# Revit family: Drapery_Track-Lutron-Curved-Ceiling_Recessed_Mount new
name_source: partatom
category: Specialty Equipment
revit_build: Autodesk Revit 2017 (Build: 20160225_1515(x64)
units: mm (PartAtom-declared; Revit-internal decimal feet)

## family parameters
Cut with Voids When Loaded = Yes
Host = Face
OmniClass Number = 23.30.60.14.21
OmniClass Title = Shades
Part Type = Normal
Room Calculation Point = No
Round Connector Dimension = Use Diameter
Shared = No

## types (6) — shared parameters
Apparent Load = 0 VA
Assembly Code = E2010320
C Recessed Ends = 0' - 0 39/64"
Default Elevation = 0' - 0"
Electronic Drive Unit D105 = Yes
Electronic Drive Unit D145 = No
Electronic Drive Unit D175 = No
Electronic Drive Unit Note = Electronic Drive Unit D105 - Carries draperies up to 105 lbs
Finish = Metal - Lutron - White
Instruction Sheet Link = http://www.lutron.com
Manufacturer = Lutron Electronics Co., Inc
Manufacturer Fax Number = 610-282-1243
Number of Poles = 1
Power Factor = 1
Product Documentation Link = http://www.lutron.com
Product Name = Traditional Drapery Track System
Product Page URL = http://www.lutron.com
Radius = 1' - 8"
Series = Sivoia QS
URL = http://www.lutron.com
Version = 2017 - v1.0a
Voltage = 24 V
Voltage Comment = 24-36V
Warranty URL = http://www.lutron.com
Wattage = 41 W
zero-valued in all types: Cost

## per-type parameters (varying)
| type | C 2nd Drapery | C Recessed | C Recessed Tandem | Ceiling Mounted | Ceiling Not Tandem | Ceiling Tandem | Center Draw | Constraints | Description | Load Classification | Not Tandem | Recessed Mount | Recessed Not Tandem | Recessed Tandem | Single Side Draw | Tandem Draw | Type Comments |
| Curve Ceiling Mounted - Tandem Draw | Yes | 0' - 1 1/16" | 0' - 1 1/16" | Yes | No | Yes | No | 3 | Curve Ceiling Mounted Traditional Drapery Track System | Other | No | No | No | No | No | Yes | Custom Lengths Up To 150'' |
| Curve Ceiling Mounted - Center Draw | Yes | 0' - 1 1/16" | 0' - 1 1/16" | Yes | Yes | No | Yes | 2 | Curve Ceiling Mounted Traditional Drapery Track System | Other | Yes | No | No | No | No | No | Custom Lengths Up To 150'' |
| Curve Ceiling Mounted - Left or Right Side Draw | No | 0' - 1 1/16" | 0' - 1 1/16" | Yes | Yes | No | No | 1 | Curve Ceiling Mounted Traditional Drapery Track System | Motor | Yes | No | No | No | Yes | No |  |
| Curve Recessed Mounted - Center Draw | Yes | 0' - 0" | 0' - 1 1/16" | No | No | No | Yes | 2 | Curve Recessed Mounted Traditional Drapery Track System | Other | Yes | Yes | Yes | No | No | No | Custom Lengths Up To 150'' |
| Curve Recessed Mounted - Left or Right Side Draw | No | 0' - 0" | 0' - 1 1/16" | No | No | No | No | 1 | Curve Recessed Mounted Traditional Drapery Track System | Other | Yes | Yes | Yes | No | Yes | No | Custom Lengths Up To 150'' |
| Curve Recessed Mounted - Tandem Draw | Yes | 0' - 0" | 0' - 0" | No | No | No | No | 3 | Curve Recessed Mounted Traditional Drapery Track System | Other | No | Yes | No | Yes | No | Yes | Custom Lengths Up To 150'' |

note: column(s) folded — value = type name in every type: Model

## geometry (parser evidence)
native form markers: Sweep x10
no freeform markers — native parametric forms only
